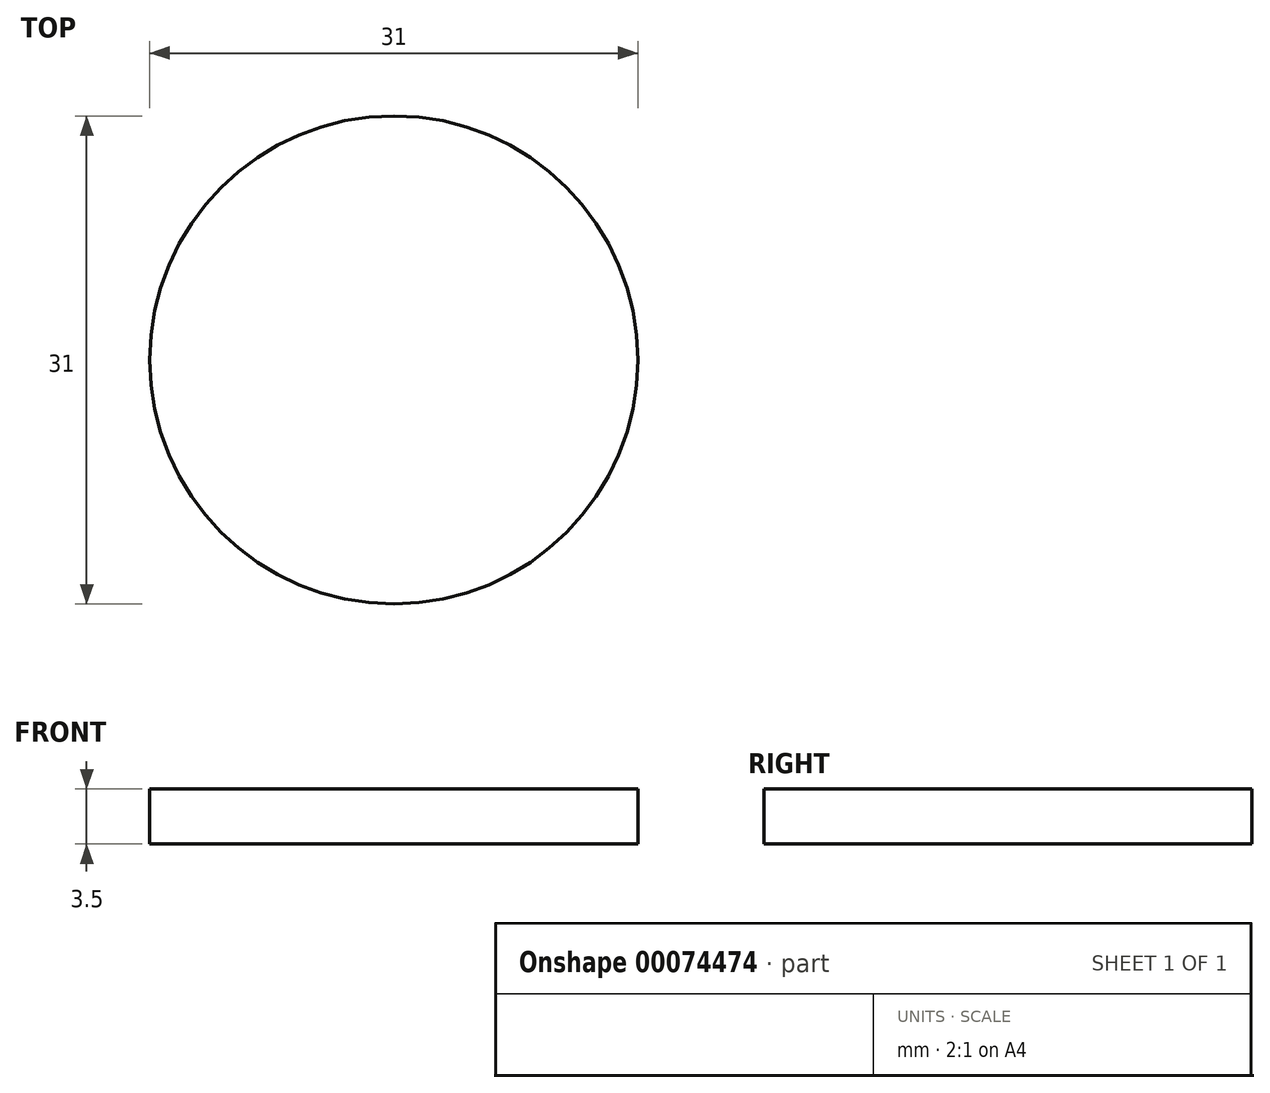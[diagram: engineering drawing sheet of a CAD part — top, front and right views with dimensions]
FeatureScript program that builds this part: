
annotation { "Feature Type Name" : "Feature", "Feature Type Description" : "" }
export const myFeature = defineFeature(function(context is Context, id is Id, definition is map)
    precondition{}
    {
        {
            var Q0;
            Q0=qCreatedBy(makeId("Top.planeOp"),FACE);
            var sketch = newSketch(context, id + "F0", { "sketchPlane" : qUnion([Q0])});
            skCircle(sketch, "E0", {"center": v(0, 0) * mm, "radius": 15.5 * mm});
            skSolve(sketch);
        }
        {
            var Q0;
            Q0 = qSketchRegion(id + "F0", true);
            extrude(context, id + "F1", {"entities" : qUnion([Q0]), "depth" : 3.5 * mm});
        }
    });
